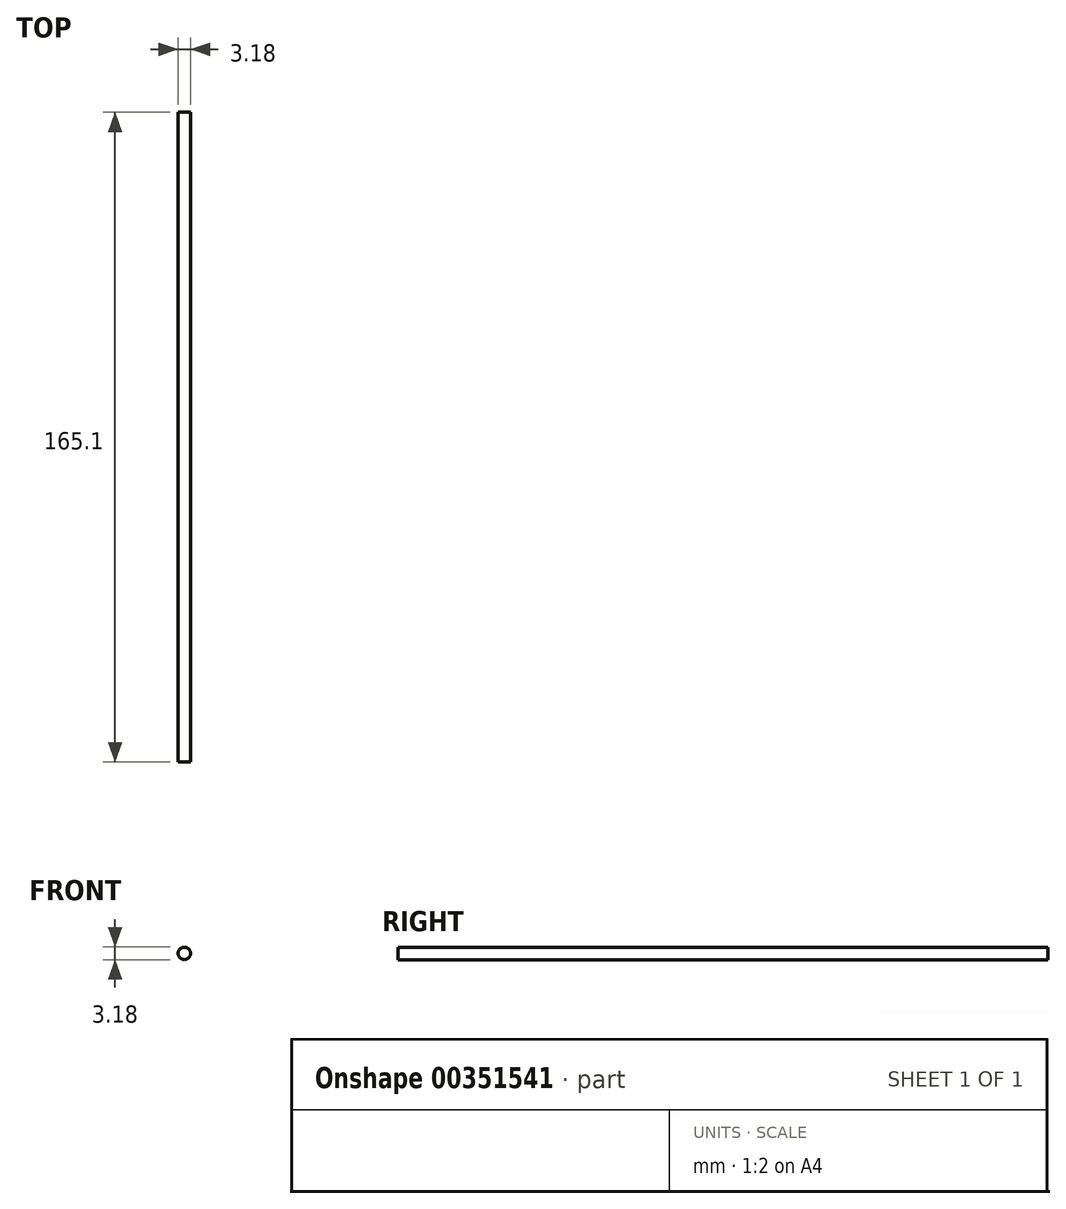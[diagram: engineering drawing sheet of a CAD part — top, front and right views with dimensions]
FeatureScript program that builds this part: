
annotation { "Feature Type Name" : "Feature", "Feature Type Description" : "" }
export const myFeature = defineFeature(function(context is Context, id is Id, definition is map)
    precondition{}
    {
        {
            var Q0;
            Q0=qCreatedBy(makeId("Front.planeOp"),FACE);
            var sketch = newSketch(context, id + "F0", { "sketchPlane" : qUnion([Q0])});
            skCircle(sketch, "E0", {"center": v(0, 0) * mm, "radius": 1.59 * mm});
            skSolve(sketch);
        }
        {
            var Q0;
            Q0 = qSketchRegion(id + "F0", true);
            extrude(context, id + "F1", {"entities" : qUnion([Q0]), "depth" : 165.1 * mm, "symmetric" : true});
        }
    });
